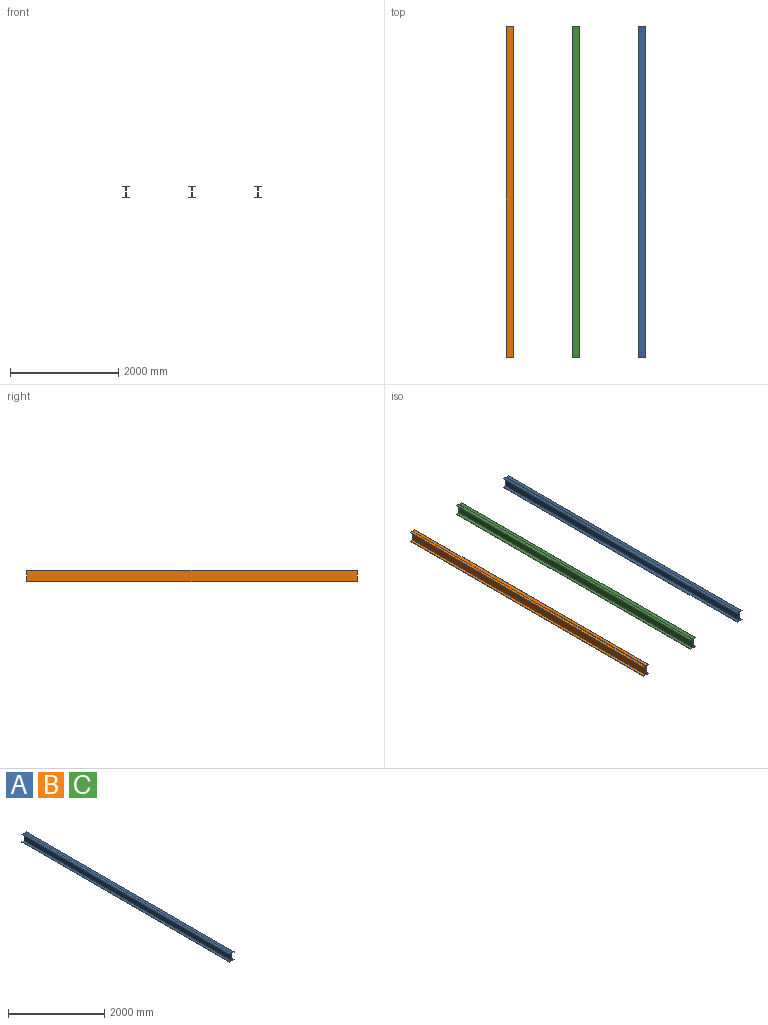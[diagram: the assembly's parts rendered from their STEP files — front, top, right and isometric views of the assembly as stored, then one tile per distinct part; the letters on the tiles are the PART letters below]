
ASSEMBLY  parts=3 mates=6
PART A: 14 faces, bbox 127x6096x203.2 mm
  f0: plane 6096x7.62mm, normal (-1,0,0), area 46451.5mm2, adj f1,f11,f12,f13
  f1: plane 6096x127mm, normal (0,0,-1), area 774192mm2, adj f0,f2,f12,f13
  f2: plane 6096x7.62mm, normal (1,0,0), area 46451.5mm2, adj f1,f3,f12,f13
  f3: plane 6096x58.74mm, normal (0,0,1), area 358063.8mm2, adj f2,f4,f12,f13
  f4: plane 6096x187.96mm, normal (1,0,0), area 1145804.2mm2, adj f3,f5,f12,f13
  f5: plane 6096x58.74mm, normal (0,0,-1), area 358063.8mm2, adj f4,f6,f12,f13
  f6: plane 6096x7.62mm, normal (1,0,0), area 46451.5mm2, adj f5,f7,f12,f13
  f7: plane 6096x127mm, normal (0,0,1), area 774192mm2, adj f6,f8,f12,f13
  f8: plane 6096x7.62mm, normal (-1,0,0), area 46451.5mm2, adj f7,f9,f12,f13
  f9: plane 6096x58.74mm, normal (0,0,-1), area 358063.8mm2, adj f8,f10,f12,f13
  f10: plane 6096x187.96mm, normal (-1,0,0), area 1145804.2mm2, adj f9,f11,f12,f13
  f11: plane 6096x58.74mm, normal (0,0,1), area 358063.8mm2, adj f0,f10,f12,f13
  f12: plane 203.2x127mm, normal (0,-1,0), area 3725.8mm2, adj f0,f1,f2,f3,f4,f5,f6,f7
  f13: plane 203.2x127mm, normal (0,1,0), area 3725.8mm2, adj f0,f1,f2,f3,f4,f5,f6,f7
PART B: same geometry as A
PART C: same geometry as A
PLACE A t=(-1972.41,-1091.91,1251.81)mm
PLACE B t=(-4410.81,-1091.91,1251.81)mm
PLACE C t=(-3191.61,-1091.91,1251.81)mm fixed
MATE planar A.f1 <-> C.f1  axis (0,0,1) through (-1908.91,-4139.91,1251.81)mm
MATE planar B.f7 <-> A.f7  axis (0,0,1) through (-4410.81,-1091.91,1455.01)mm
MATE planar C.f12 <-> B.f12  axis (0,-1,0) through (-3191.61,-4139.91,1455.01)mm
MATE planar B.f7 <-> C.f7  axis (0,0,1) through (-4410.81,-1091.91,1455.01)mm
MATE planar C.f1 <-> B.f1  axis (0,0,1) through (-3128.11,-4139.91,1251.81)mm
MATE planar B.f12 <-> A.f12  axis (0,-1,0) through (-4406.05,-4139.91,1447.39)mm
